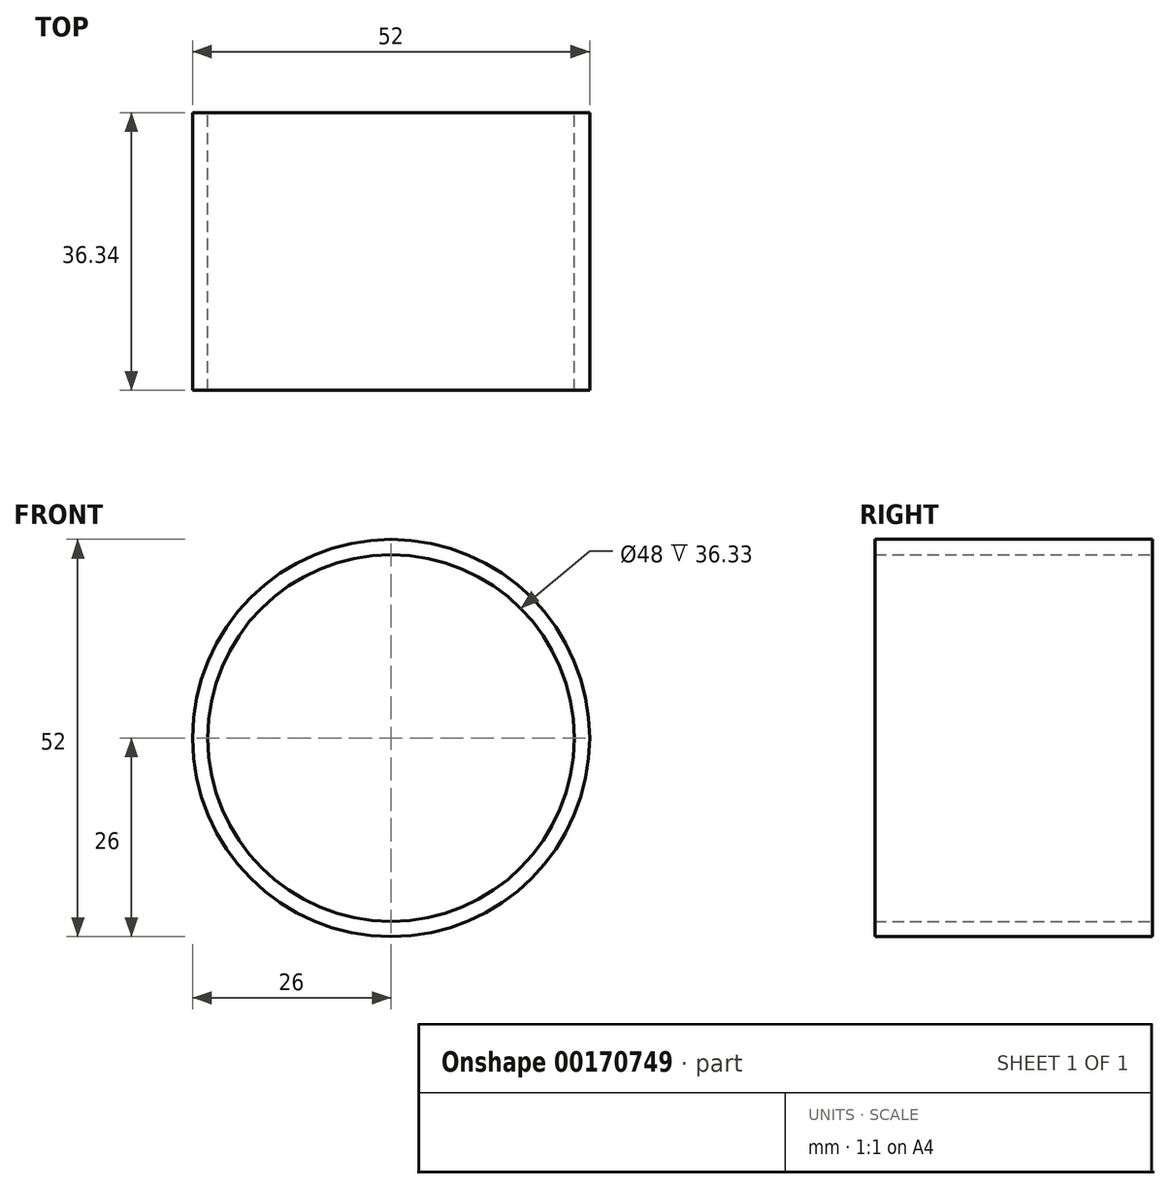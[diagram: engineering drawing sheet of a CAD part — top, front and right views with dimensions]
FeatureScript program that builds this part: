
annotation { "Feature Type Name" : "Feature", "Feature Type Description" : "" }
export const myFeature = defineFeature(function(context is Context, id is Id, definition is map)
    precondition{}
    {
        {
            var Q0;
            Q0=qCreatedBy(makeId("Front.planeOp"),FACE);
            var sketch = newSketch(context, id + "F0", { "sketchPlane" : qUnion([Q0])});
            skCircle(sketch, "E0", {"center": v(0, 0) * mm, "radius": 26 * mm});
            skCircle(sketch, "E1", {"center": v(0, 0) * mm, "radius": 24 * mm});
            skSolve(sketch);
        }
        {
            var Q0;
            Q0=qSketchRegion(id+"F0",true);
            extrude(context, id + "F1", {"entities" : qUnion([Q0]), "flatOperationType" : FlatOperationType.REMOVE, "offsetDistance" : 25 * mm, "depth" : 36.33 * mm, "domain" : OperationDomain.MODEL, "symmetric" : true});
        }
    });
